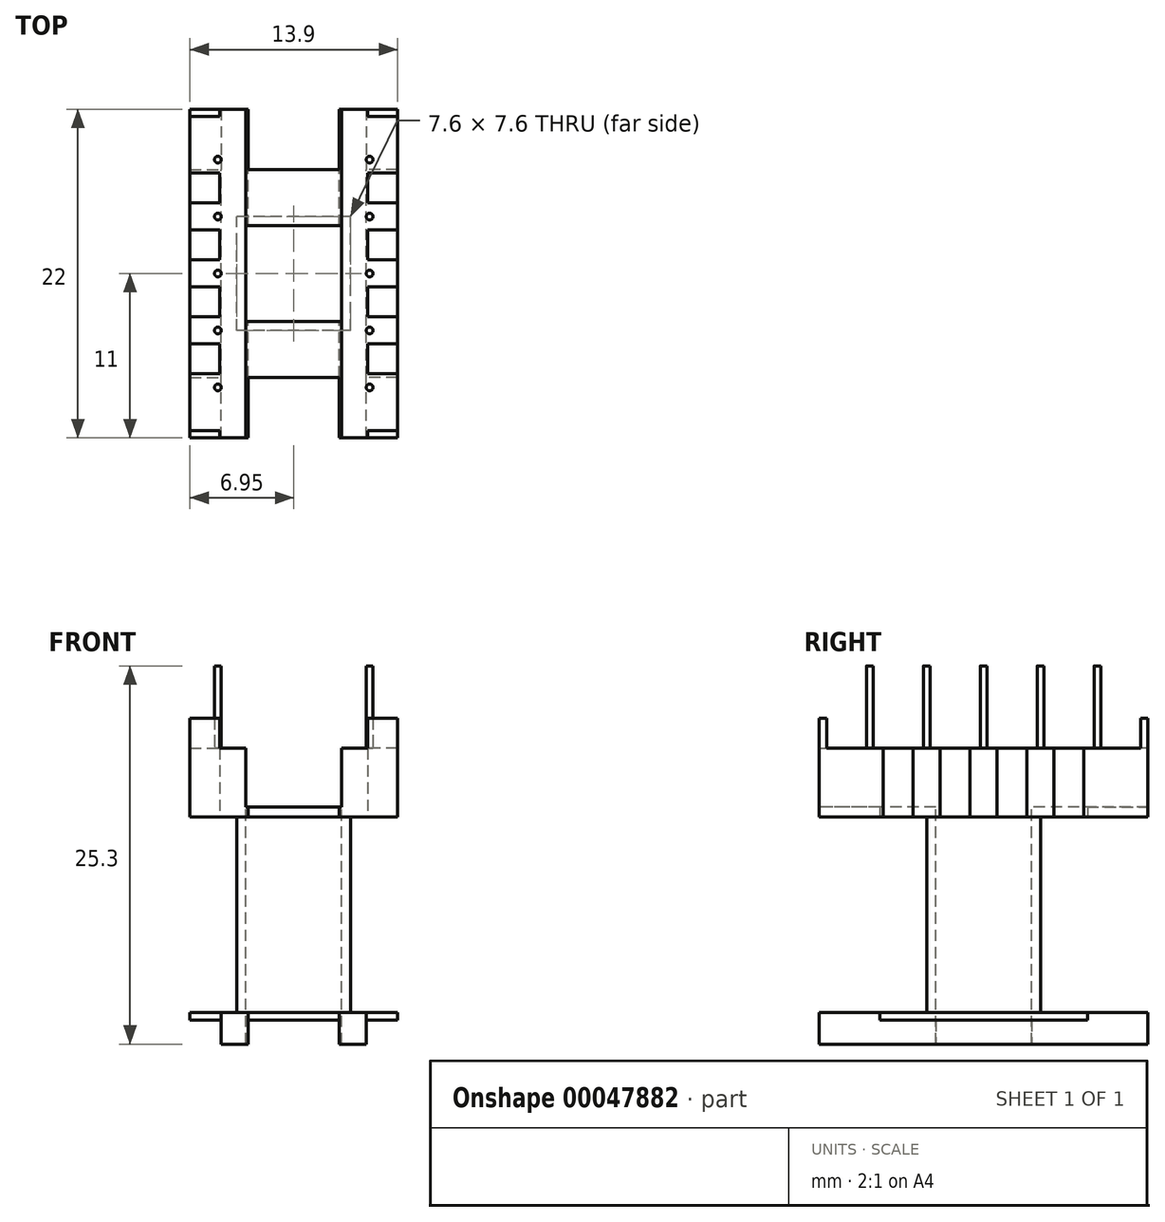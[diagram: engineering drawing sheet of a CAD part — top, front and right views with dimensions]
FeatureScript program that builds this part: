
annotation { "Feature Type Name" : "Feature", "Feature Type Description" : "" }
export const myFeature = defineFeature(function(context is Context, id is Id, definition is map)
    precondition{}
    {
        {
            var Q0;
            Q0=qCreatedBy(makeId("Top.planeOp"),FACE);
            var sketch = newSketch(context, id + "F0", { "sketchPlane" : qUnion([Q0])});
            skLineSegment(sketch, "E0.bottom", {"start": v(-6.95, -11) * mm, "end": v(6.95, -11) * mm});
            skLineSegment(sketch, "E0.top", {"start": v(-6.95, 11) * mm, "end": v(6.95, 11) * mm});
            skLineSegment(sketch, "E0.left", {"start": v(-6.95, -11) * mm, "end": v(-6.95, 11) * mm});
            skLineSegment(sketch, "E0.right", {"start": v(6.95, -11) * mm, "end": v(6.95, 11) * mm});
            skSolve(sketch);
        }
        {
            var Q0;
            Q0 = qSketchRegion(id + "F0", true);
            extrude(context, id + "F1", {"entities" : qUnion([Q0]), "depth" : 19.8 * mm});
        }
        {
            var Q0;
            Q0=makeQuery(id+"F1.opExtrude","CAP_FACE",FACE,{"disambiguationData":[OSD([sQuery(id+"F0.wireOp",EDGE,"E0.bottom"),sQuery(id+"F0.wireOp",EDGE,"E0.top"),sQuery(id+"F0.wireOp",EDGE,"E0.left"),sQuery(id+"F0.wireOp",EDGE,"E0.right")])],"isStart":true});
            cPlane(context, id + "F2", {"entities" : qUnion([Q0]), "cplaneType" : CPlaneType.OFFSET, "offset" : 2.1 * mm, "oppositeDirection" : true, "width" : 150 * mm, "height" : 150 * mm});
        }
        {
            var Q0;
            Q0=qCreatedBy(id+"F2.planeOp",FACE);
            cPlane(context, id + "F3", {"entities" : qUnion([Q0]), "cplaneType" : CPlaneType.OFFSET, "offset" : 13.1 * mm, "oppositeDirection" : true, "width" : 150 * mm, "height" : 150 * mm});
        }
        {
            var Q0;
            Q0=qCreatedBy(id+"F2.planeOp",FACE);
            var sketch = newSketch(context, id + "F4", { "sketchPlane" : qUnion([Q0])});
            skLineSegment(sketch, "E1.bottom", {"start": v(-3.8, -3.8) * mm, "end": v(3.8, -3.8) * mm});
            skLineSegment(sketch, "E1.top", {"start": v(-3.8, 3.8) * mm, "end": v(3.8, 3.8) * mm});
            skLineSegment(sketch, "E1.left", {"start": v(-3.8, -3.8) * mm, "end": v(-3.8, 3.8) * mm});
            skLineSegment(sketch, "E1.right", {"start": v(3.8, -3.8) * mm, "end": v(3.8, 3.8) * mm});
            skLineSegment(sketch, "E2.0", {"start": v(6.95, 11) * mm, "end": v(6.95, -11) * mm});
            skLineSegment(sketch, "E3.0", {"start": v(-6.95, 11) * mm, "end": v(6.95, 11) * mm});
            skLineSegment(sketch, "E4.0.0", {"start": v(-6.95, -11) * mm, "end": v(-6.95, 11) * mm});
            skLineSegment(sketch, "E4.0.2", {"start": v(-6.95, 11) * mm, "end": v(-6.95, -11) * mm});
            skLineSegment(sketch, "E4.1.2", {"start": v(6.95, 11) * mm, "end": v(-6.95, 11) * mm});
            skLineSegment(sketch, "E4.2.2", {"start": v(6.95, -11) * mm, "end": v(6.95, 11) * mm});
            skLineSegment(sketch, "E4.3.0", {"start": v(6.95, -11) * mm, "end": v(-6.95, -11) * mm});
            skLineSegment(sketch, "E4.3.2", {"start": v(-6.95, -11) * mm, "end": v(6.95, -11) * mm});
            skSolve(sketch);
        }
        {
            var Q0;
            Q0 = qSketchRegion(id + "F4", true);
            var Q1;
            Q1=qCreatedBy(id+"F3.planeOp",FACE);
            extrude(context, id + "F5", {"entities" : qUnion([Q0]), "operationType" : NewBodyOperationType.REMOVE, "endBound" : BoundingType.UP_TO_SURFACE, "oppositeDirection" : true, "endBoundEntityFace" : qUnion([Q1]), "depth" : 25 * mm});
        }
        {
            var Q0;
            Q0=makeQuery(id+"F1.opExtrude","CAP_FACE",FACE,{"disambiguationData":[OSD([sQuery(id+"F0.wireOp",EDGE,"E0.bottom"),sQuery(id+"F0.wireOp",EDGE,"E0.top"),sQuery(id+"F0.wireOp",EDGE,"E0.left"),sQuery(id+"F0.wireOp",EDGE,"E0.right")])],"isStart":false});
            var sketch = newSketch(context, id + "F6", { "sketchPlane" : qUnion([Q0])});
            skLineSegment(sketch, "E5.0.3", {"start": v(-3.8, 3.8) * mm, "end": v(3.8, 3.8) * mm, "construction": true});
            skLineSegment(sketch, "E5.1.2", {"start": v(-3.8, 3.8) * mm, "end": v(-3.8, -3.8) * mm, "construction": true});
            skLineSegment(sketch, "E5.2.2", {"start": v(-3.8, -3.8) * mm, "end": v(3.8, -3.8) * mm, "construction": true});
            skLineSegment(sketch, "E5.3.3", {"start": v(3.8, 3.8) * mm, "end": v(3.8, -3.8) * mm, "construction": true});
            skLineSegment(sketch, "E6.0", {"start": v(-3.2, 3.2) * mm, "end": v(-3.2, -3.2) * mm});
            skLineSegment(sketch, "E6.1", {"start": v(-3.2, 3.2) * mm, "end": v(3.2, 3.2) * mm});
            skLineSegment(sketch, "E6.2", {"start": v(3.2, 3.2) * mm, "end": v(3.2, -3.2) * mm});
            skLineSegment(sketch, "E6.3", {"start": v(-3.2, -3.2) * mm, "end": v(3.2, -3.2) * mm});
            skSolve(sketch);
        }
        {
            var Q0;
            Q0 = qSketchRegion(id + "F6", true);
            var Q1;
            Q1 = qConstructionFilter(qBodyType(qCreatedBy(id + "F6" ,EDGE), BodyType.WIRE), ConstructionObject.NO);
            extrude(context, id + "F7", {"entities" : qUnion([Q0]), "operationType" : NewBodyOperationType.REMOVE, "surfaceEntities" : qUnion([Q1]), "endBound" : BoundingType.THROUGH_ALL, "oppositeDirection" : true, "depth" : 25 * mm});
        }
        {
            var Q0;
            Q0=makeQuery(id+"F1.opExtrude","CAP_FACE",FACE,{"disambiguationData":[OSD([sQuery(id+"F0.wireOp",EDGE,"E0.bottom"),sQuery(id+"F0.wireOp",EDGE,"E0.top"),sQuery(id+"F0.wireOp",EDGE,"E0.left"),sQuery(id+"F0.wireOp",EDGE,"E0.right")])],"isStart":true});
            var sketch = newSketch(context, id + "F8", { "sketchPlane" : qUnion([Q0])});
            skLineSegment(sketch, "E7.0", {"start": v(-6.95, 11) * mm, "end": v(6.95, 11) * mm, "construction": true});
            skLineSegment(sketch, "E8.0", {"start": v(-6.95, -11) * mm, "end": v(6.95, -11) * mm, "construction": true});
            skLineSegment(sketch, "E9.0.1", {"start": v(6.95, 11) * mm, "end": v(-6.95, 11) * mm, "construction": true});
            skLineSegment(sketch, "E10.0.3", {"start": v(6.95, -11) * mm, "end": v(-6.95, -11) * mm, "construction": true});
            skLineSegment(sketch, "E11.0.1", {"start": v(-6.95, 11) * mm, "end": v(-6.95, -11) * mm, "construction": true});
            skLineSegment(sketch, "E11.0.3", {"start": v(-6.95, -11) * mm, "end": v(-6.95, 11) * mm, "construction": true});
            skLineSegment(sketch, "E12.0.1", {"start": v(6.95, -11) * mm, "end": v(6.95, 11) * mm, "construction": true});
            skLineSegment(sketch, "E12.0.3", {"start": v(6.95, 11) * mm, "end": v(6.95, -11) * mm, "construction": true});
            skLineSegment(sketch, "E13.bottom", {"start": v(-4.85, 11) * mm, "end": v(-3.05, 11) * mm, "construction": true});
            skLineSegment(sketch, "E13.top", {"start": v(-4.85, -11) * mm, "end": v(-3.05, -11) * mm, "construction": true});
            skLineSegment(sketch, "E13.left", {"start": v(-4.85, 11) * mm, "end": v(-4.85, -11) * mm});
            skLineSegment(sketch, "E13.right", {"start": v(-3.05, 11) * mm, "end": v(-3.05, -11) * mm});
            skLineSegment(sketch, "E14.bottom", {"start": v(3.05, 11) * mm, "end": v(4.85, 11) * mm, "construction": true});
            skLineSegment(sketch, "E14.top", {"start": v(3.05, -11) * mm, "end": v(4.85, -11) * mm, "construction": true});
            skLineSegment(sketch, "E14.left", {"start": v(3.05, 11) * mm, "end": v(3.05, -11) * mm});
            skLineSegment(sketch, "E14.right", {"start": v(4.85, 11) * mm, "end": v(4.85, -11) * mm});
            skLineSegment(sketch, "E15", {"start": v(-3.05, 11) * mm, "end": v(3.05, 11) * mm});
            skLineSegment(sketch, "E16", {"start": v(-3.05, -11) * mm, "end": v(3.05, -11) * mm});
            skLineSegment(sketch, "E17", {"start": v(4.85, -11) * mm, "end": v(6.95, -11) * mm});
            skLineSegment(sketch, "E18", {"start": v(6.95, 11) * mm, "end": v(6.95, -11) * mm});
            skLineSegment(sketch, "E19", {"start": v(6.95, 11) * mm, "end": v(4.85, 11) * mm});
            skLineSegment(sketch, "E20", {"start": v(-4.85, 11) * mm, "end": v(-6.95, 11) * mm});
            skLineSegment(sketch, "E21", {"start": v(-6.95, 11) * mm, "end": v(-6.95, -11) * mm});
            skLineSegment(sketch, "E22", {"start": v(-6.95, -11) * mm, "end": v(-4.85, -11) * mm});
            skSolve(sketch);
        }
        {
            var Q0;
            Q0 = qSketchRegion(id + "F8", true);
            var Q1;
            Q1=sQuery(id+"F8.wireOp",EDGE,"E13.bottom");
            var Q2;
            Q2=sQuery(id+"F8.wireOp",EDGE,"E13.top");
            var Q3;
            Q3=sQuery(id+"F8.wireOp",EDGE,"E14.bottom");
            var Q4;
            Q4=sQuery(id+"F8.wireOp",EDGE,"E14.top");
            var Q5;
            Q5=makeQuery(id+"F5.boolean.opBoolean","COPY",FACE,{"derivedFrom":makeQuery(id+"F5.opExtrude","CAP_FACE",FACE,{"disambiguationData":[OSD([sQuery(id+"F4.wireOp",EDGE,"E1.bottom"),sQuery(id+"F4.wireOp",EDGE,"E1.top"),sQuery(id+"F4.wireOp",EDGE,"E1.left"),sQuery(id+"F4.wireOp",EDGE,"E1.right"),sQuery(id+"F4.wireOp",EDGE,"E4.0.2"),sQuery(id+"F4.wireOp",EDGE,"E4.1.2"),sQuery(id+"F4.wireOp",EDGE,"E4.2.2"),sQuery(id+"F4.wireOp",EDGE,"E4.3.2")])],"isStart":true})});
            extrude(context, id + "F9", {"entities" : qUnion([Q0]), "operationType" : NewBodyOperationType.REMOVE, "surfaceEntities" : qUnion([Q1, Q2, Q3, Q4]), "oppositeDirection" : true, "endBoundEntityFace" : qUnion([Q5]), "depth" : 1.6 * mm});
        }
        {
            var Q0;
            Q0=makeQuery(id+"F5.boolean.opBoolean","COPY",FACE,{"derivedFrom":makeQuery(id+"F5.opExtrude","CAP_FACE",FACE,{"disambiguationData":[OSD([sQuery(id+"F4.wireOp",EDGE,"E1.bottom"),sQuery(id+"F4.wireOp",EDGE,"E1.top"),sQuery(id+"F4.wireOp",EDGE,"E1.left"),sQuery(id+"F4.wireOp",EDGE,"E1.right"),sQuery(id+"F4.wireOp",EDGE,"E4.0.2"),sQuery(id+"F4.wireOp",EDGE,"E4.1.2"),sQuery(id+"F4.wireOp",EDGE,"E4.2.2"),sQuery(id+"F4.wireOp",EDGE,"E4.3.2")])],"isStart":true})});
            var sketch = newSketch(context, id + "F10", { "sketchPlane" : qUnion([Q0])});
            skPoint(sketch, "E23.0", {"position": v(6.95, 11) * mm});
            skPoint(sketch, "E23.1", {"position": v(4.85, 11) * mm});
            skPoint(sketch, "E23.2", {"position": v(3.05, 11) * mm});
            skPoint(sketch, "E23.3", {"position": v(-3.05, 11) * mm});
            skPoint(sketch, "E23.4", {"position": v(-4.85, 11) * mm});
            skPoint(sketch, "E23.5", {"position": v(-6.95, 11) * mm});
            skPoint(sketch, "E23.6", {"position": v(6.95, -11) * mm});
            skPoint(sketch, "E23.7", {"position": v(4.85, -11) * mm});
            skPoint(sketch, "E23.8", {"position": v(3.05, -11) * mm});
            skPoint(sketch, "E23.9", {"position": v(-4.85, -11) * mm});
            skPoint(sketch, "E23.10", {"position": v(-6.95, -11) * mm});
            skPoint(sketch, "E23.11", {"position": v(-3.05, -11) * mm});
            skLineSegment(sketch, "E24.bottom", {"start": v(6.95, 11) * mm, "end": v(4.85, 11) * mm});
            skLineSegment(sketch, "E24.top", {"start": v(6.95, 6.95) * mm, "end": v(4.85, 6.95) * mm});
            skLineSegment(sketch, "E24.left", {"start": v(6.95, 11) * mm, "end": v(6.95, 6.95) * mm});
            skLineSegment(sketch, "E24.right", {"start": v(4.85, 11) * mm, "end": v(4.85, 6.95) * mm});
            skLineSegment(sketch, "E25.bottom", {"start": v(6.95, -11) * mm, "end": v(4.85, -11) * mm});
            skLineSegment(sketch, "E25.top", {"start": v(6.95, -6.95) * mm, "end": v(4.85, -6.95) * mm});
            skLineSegment(sketch, "E25.left", {"start": v(6.95, -11) * mm, "end": v(6.95, -6.95) * mm});
            skLineSegment(sketch, "E25.right", {"start": v(4.85, -11) * mm, "end": v(4.85, -6.95) * mm});
            skLineSegment(sketch, "E26.bottom", {"start": v(3.05, -11) * mm, "end": v(-3.05, -11) * mm});
            skLineSegment(sketch, "E26.top", {"start": v(3.05, -6.95) * mm, "end": v(-3.05, -6.95) * mm});
            skLineSegment(sketch, "E26.left", {"start": v(3.05, -11) * mm, "end": v(3.05, -6.95) * mm});
            skLineSegment(sketch, "E26.right", {"start": v(-3.05, -11) * mm, "end": v(-3.05, -6.95) * mm});
            skLineSegment(sketch, "E27.bottom", {"start": v(-6.95, -11) * mm, "end": v(-4.85, -11) * mm});
            skLineSegment(sketch, "E27.top", {"start": v(-6.95, -6.95) * mm, "end": v(-4.85, -6.95) * mm});
            skLineSegment(sketch, "E27.left", {"start": v(-6.95, -11) * mm, "end": v(-6.95, -6.95) * mm});
            skLineSegment(sketch, "E27.right", {"start": v(-4.85, -11) * mm, "end": v(-4.85, -6.95) * mm});
            skLineSegment(sketch, "E28.bottom", {"start": v(-6.95, 11) * mm, "end": v(-4.85, 11) * mm});
            skLineSegment(sketch, "E28.top", {"start": v(-6.95, 6.95) * mm, "end": v(-4.85, 6.95) * mm});
            skLineSegment(sketch, "E28.left", {"start": v(-6.95, 11) * mm, "end": v(-6.95, 6.95) * mm});
            skLineSegment(sketch, "E28.right", {"start": v(-4.85, 11) * mm, "end": v(-4.85, 6.95) * mm});
            skLineSegment(sketch, "E29.bottom", {"start": v(-3.05, 11) * mm, "end": v(3.05, 11) * mm});
            skLineSegment(sketch, "E29.top", {"start": v(-3.05, 6.95) * mm, "end": v(3.05, 6.95) * mm});
            skLineSegment(sketch, "E29.left", {"start": v(-3.05, 11) * mm, "end": v(-3.05, 6.95) * mm});
            skLineSegment(sketch, "E29.right", {"start": v(3.05, 11) * mm, "end": v(3.05, 6.95) * mm});
            skSolve(sketch);
        }
        {
            var Q0;
            Q0 = qSketchRegion(id + "F10", true);
            var Q1;
            Q1=makeQuery(id+"F9.boolean.opBoolean","COPY",FACE,{"disambiguationData":[OD(0.0)],"derivedFrom":makeQuery(id+"F9.opExtrude","CAP_FACE",FACE,{"disambiguationData":[OSD([sQuery(id+"F8.wireOp",EDGE,"E13.right"),sQuery(id+"F8.wireOp",EDGE,"E14.left"),sQuery(id+"F8.wireOp",EDGE,"E15"),sQuery(id+"F8.wireOp",EDGE,"E16")])],"isStart":false})});
            extrude(context, id + "F11", {"entities" : qUnion([Q0]), "operationType" : NewBodyOperationType.REMOVE, "endBound" : BoundingType.UP_TO_SURFACE, "oppositeDirection" : true, "endBoundEntityFace" : qUnion([Q1]), "depth" : 25 * mm});
        }
        {
            var Q0;
            Q0=makeQuery(id+"F5.boolean.opBoolean","COPY",FACE,{"derivedFrom":makeQuery(id+"F5.opExtrude","CAP_FACE",FACE,{"disambiguationData":[OSD([sQuery(id+"F4.wireOp",EDGE,"E1.bottom"),sQuery(id+"F4.wireOp",EDGE,"E1.top"),sQuery(id+"F4.wireOp",EDGE,"E1.left"),sQuery(id+"F4.wireOp",EDGE,"E1.right"),sQuery(id+"F4.wireOp",EDGE,"E4.0.2"),sQuery(id+"F4.wireOp",EDGE,"E4.1.2"),sQuery(id+"F4.wireOp",EDGE,"E4.2.2"),sQuery(id+"F4.wireOp",EDGE,"E4.3.2")])],"isStart":false})});
            var sketch = newSketch(context, id + "F12", { "sketchPlane" : qUnion([Q0])});
            skPoint(sketch, "E30.0", {"position": v(6.95, -11) * mm});
            skPoint(sketch, "E30.1", {"position": v(-6.95, -11) * mm});
            skPoint(sketch, "E30.2", {"position": v(6.95, 11) * mm});
            skPoint(sketch, "E30.3", {"position": v(-6.95, 11) * mm});
            skPoint(sketch, "E30.5", {"position": v(3.05, 6.95) * mm});
            skPoint(sketch, "E30.6", {"position": v(3.05, -6.95) * mm});
            skPoint(sketch, "E30.7", {"position": v(-3.05, -6.95) * mm});
            skLineSegment(sketch, "E31.bottom", {"start": v(-3.05, -6.95) * mm, "end": v(3.05, -6.95) * mm});
            skLineSegment(sketch, "E31.top", {"start": v(-3.05, -11) * mm, "end": v(3.05, -11) * mm});
            skLineSegment(sketch, "E31.left", {"start": v(-3.05, -6.95) * mm, "end": v(-3.05, -11) * mm});
            skLineSegment(sketch, "E31.right", {"start": v(3.05, -6.95) * mm, "end": v(3.05, -11) * mm});
            skLineSegment(sketch, "E32", {"start": v(-6.95, 11) * mm, "end": v(-6.95, -11) * mm, "construction": true});
            skLineSegment(sketch, "E33.bottom", {"start": v(6.95, -6.72) * mm, "end": v(4.95, -6.72) * mm});
            skLineSegment(sketch, "E33.top", {"start": v(6.95, -4.72) * mm, "end": v(4.95, -4.72) * mm});
            skLineSegment(sketch, "E33.left", {"start": v(6.95, -6.72) * mm, "end": v(6.95, -4.72) * mm});
            skLineSegment(sketch, "E33.right", {"start": v(4.95, -6.72) * mm, "end": v(4.95, -4.72) * mm});
            skLineSegment(sketch, "E34.bottom", {"start": v(6.95, -2.9) * mm, "end": v(4.95, -2.9) * mm});
            skLineSegment(sketch, "E34.top", {"start": v(6.95, -0.9) * mm, "end": v(4.95, -0.9) * mm});
            skLineSegment(sketch, "E34.left", {"start": v(6.95, -2.9) * mm, "end": v(6.95, -0.9) * mm});
            skLineSegment(sketch, "E34.right", {"start": v(4.95, -2.9) * mm, "end": v(4.95, -0.9) * mm});
            skLineSegment(sketch, "E35.bottom", {"start": v(6.95, 0.9) * mm, "end": v(4.95, 0.9) * mm});
            skLineSegment(sketch, "E35.top", {"start": v(6.95, 2.9) * mm, "end": v(4.95, 2.9) * mm});
            skLineSegment(sketch, "E35.left", {"start": v(6.95, 0.9) * mm, "end": v(6.95, 2.9) * mm});
            skLineSegment(sketch, "E35.right", {"start": v(4.95, 0.9) * mm, "end": v(4.95, 2.9) * mm});
            skLineSegment(sketch, "E36.bottom", {"start": v(6.95, 4.72) * mm, "end": v(4.95, 4.72) * mm});
            skLineSegment(sketch, "E36.top", {"start": v(6.95, 6.72) * mm, "end": v(4.95, 6.72) * mm});
            skLineSegment(sketch, "E36.left", {"start": v(6.95, 4.72) * mm, "end": v(6.95, 6.72) * mm});
            skLineSegment(sketch, "E36.right", {"start": v(4.95, 4.72) * mm, "end": v(4.95, 6.72) * mm});
            skLineSegment(sketch, "E37", {"start": v(6.95, -4.72) * mm, "end": v(6.95, -2.9) * mm, "construction": true});
            skLineSegment(sketch, "E38", {"start": v(6.95, -0.9) * mm, "end": v(6.95, 0.9) * mm, "construction": true});
            skLineSegment(sketch, "E39", {"start": v(6.95, 2.9) * mm, "end": v(6.95, 4.72) * mm, "construction": true});
            skLineSegment(sketch, "E40.bottom", {"start": v(-6.95, 6.72) * mm, "end": v(-4.95, 6.72) * mm});
            skLineSegment(sketch, "E40.top", {"start": v(-6.95, 4.72) * mm, "end": v(-4.95, 4.72) * mm});
            skLineSegment(sketch, "E40.left", {"start": v(-6.95, 6.72) * mm, "end": v(-6.95, 4.72) * mm});
            skLineSegment(sketch, "E40.right", {"start": v(-4.95, 6.72) * mm, "end": v(-4.95, 4.72) * mm});
            skPoint(sketch, "E41.0", {"position": v(-3.05, 6.95) * mm});
            skLineSegment(sketch, "E42.bottom", {"start": v(3.05, 6.95) * mm, "end": v(-3.05, 6.95) * mm});
            skLineSegment(sketch, "E42.top", {"start": v(3.05, 11) * mm, "end": v(-3.05, 11) * mm});
            skLineSegment(sketch, "E42.left", {"start": v(3.05, 6.95) * mm, "end": v(3.05, 11) * mm});
            skLineSegment(sketch, "E42.right", {"start": v(-3.05, 6.95) * mm, "end": v(-3.05, 11) * mm});
            skLineSegment(sketch, "E43.bottom", {"start": v(-6.95, 2.9) * mm, "end": v(-4.95, 2.9) * mm});
            skLineSegment(sketch, "E43.top", {"start": v(-6.95, 0.9) * mm, "end": v(-4.95, 0.9) * mm});
            skLineSegment(sketch, "E43.left", {"start": v(-6.95, 2.9) * mm, "end": v(-6.95, 0.9) * mm});
            skLineSegment(sketch, "E43.right", {"start": v(-4.95, 2.9) * mm, "end": v(-4.95, 0.9) * mm});
            skLineSegment(sketch, "E44.bottom", {"start": v(-6.95, -0.9) * mm, "end": v(-4.95, -0.9) * mm});
            skLineSegment(sketch, "E44.top", {"start": v(-6.95, -2.9) * mm, "end": v(-4.95, -2.9) * mm});
            skLineSegment(sketch, "E44.left", {"start": v(-6.95, -0.9) * mm, "end": v(-6.95, -2.9) * mm});
            skLineSegment(sketch, "E44.right", {"start": v(-4.95, -0.9) * mm, "end": v(-4.95, -2.9) * mm});
            skLineSegment(sketch, "E45.bottom", {"start": v(-6.95, -4.72) * mm, "end": v(-4.95, -4.72) * mm});
            skLineSegment(sketch, "E45.top", {"start": v(-6.95, -6.72) * mm, "end": v(-4.95, -6.72) * mm});
            skLineSegment(sketch, "E45.left", {"start": v(-6.95, -4.72) * mm, "end": v(-6.95, -6.72) * mm});
            skLineSegment(sketch, "E45.right", {"start": v(-4.95, -4.72) * mm, "end": v(-4.95, -6.72) * mm});
            skLineSegment(sketch, "E46", {"start": v(-6.95, 4.72) * mm, "end": v(-6.95, 2.9) * mm, "construction": true});
            skLineSegment(sketch, "E47", {"start": v(-6.95, 0.9) * mm, "end": v(-6.95, -0.9) * mm, "construction": true});
            skLineSegment(sketch, "E48", {"start": v(-6.95, -2.9) * mm, "end": v(-6.95, -4.72) * mm, "construction": true});
            skLineSegment(sketch, "E49", {"start": v(-6.95, 2.9) * mm, "end": v(-6.95, 4.72) * mm, "construction": true});
            skSolve(sketch);
        }
        {
            var Q0;
            Q0 = qSketchRegion(id + "F12", true);
            var Q1;
            Q1=makeQuery(id+"F1.opExtrude","CAP_FACE",FACE,{"disambiguationData":[OSD([sQuery(id+"F0.wireOp",EDGE,"E0.bottom"),sQuery(id+"F0.wireOp",EDGE,"E0.top"),sQuery(id+"F0.wireOp",EDGE,"E0.left"),sQuery(id+"F0.wireOp",EDGE,"E0.right")])],"isStart":false});
            extrude(context, id + "F13", {"entities" : qUnion([Q0]), "operationType" : NewBodyOperationType.REMOVE, "endBound" : BoundingType.UP_TO_SURFACE, "oppositeDirection" : true, "endBoundEntityFace" : qUnion([Q1]), "depth" : 25 * mm});
        }
        {
            var Q0;
            Q0=qCreatedBy(makeId("Front.planeOp"),FACE);
            var sketch = newSketch(context, id + "F14", { "sketchPlane" : qUnion([Q0])});
            skLineSegment(sketch, "E50.bottom", {"start": v(3.2, 15.85) * mm, "end": v(-3.2, 15.85) * mm});
            skLineSegment(sketch, "E50.top", {"start": v(3.2, 19.8) * mm, "end": v(-3.2, 19.8) * mm});
            skLineSegment(sketch, "E50.left", {"start": v(3.2, 15.85) * mm, "end": v(3.2, 19.8) * mm});
            skLineSegment(sketch, "E50.right", {"start": v(-3.2, 15.85) * mm, "end": v(-3.2, 19.8) * mm});
            skPoint(sketch, "E51.0", {"position": v(-3.2, 19.8) * mm});
            skPoint(sketch, "E51.1", {"position": v(3.2, 19.8) * mm});
            skPoint(sketch, "E52.0", {"position": v(-3.05, 15.2) * mm});
            skPoint(sketch, "E52.1", {"position": v(3.05, 15.2) * mm});
            skSolve(sketch);
        }
        {
            var Q0;
            Q0 = qSketchRegion(id + "F14", true);
            extrude(context, id + "F15", {"entities" : qUnion([Q0]), "operationType" : NewBodyOperationType.REMOVE, "endBound" : BoundingType.THROUGH_ALL, "oppositeDirection" : true, "depth" : 25 * mm, "hasSecondDirection" : true, "secondDirectionBound" : SecondDirectionBoundingType.THROUGH_ALL, "secondDirectionOppositeDirection" : false, "secondDirectionDepth" : 25 * mm});
        }
        {
            var Q0;
            {var subQ0=sQuery(id+"F0.wireOp",EDGE,"E0.bottom");var subQ1=sQuery(id+"F0.wireOp",EDGE,"E0.top");var subQ2=sQuery(id+"F0.wireOp",EDGE,"E0.right");Q0=makeQuery(id+"F15.boolean.opBoolean","SPLIT",FACE,{"disambiguationData":[TD([makeQuery(id+"F1.opExtrude","SWEPT_FACE",FACE,{"disambiguationData":[OSD([subQ2])]})])],"derivedFrom":makeQuery(id+"F1.opExtrude","CAP_FACE",FACE,{"disambiguationData":[OSD([subQ0,subQ1,sQuery(id+"F0.wireOp",EDGE,"E0.left"),subQ2])],"isStart":false})});}
            var sketch = newSketch(context, id + "F16", { "sketchPlane" : qUnion([Q0])});
            skLineSegment(sketch, "E53", {"start": v(-5.08, -11) * mm, "end": v(-5.08, 11) * mm, "construction": true});
            skLineSegment(sketch, "E54", {"start": v(5.08, -11) * mm, "end": v(5.08, 11) * mm, "construction": true});
            skLineSegment(sketch, "E55", {"start": v(6.95, 3.81) * mm, "end": v(-5.08, 3.81) * mm, "construction": true});
            skLineSegment(sketch, "E56", {"start": v(6.95, 0) * mm, "end": v(-5.08, 0) * mm, "construction": true});
            skLineSegment(sketch, "E57", {"start": v(6.95, -3.81) * mm, "end": v(-5.08, -3.81) * mm, "construction": true});
            skLineSegment(sketch, "E58", {"start": v(5.08, 7.62) * mm, "end": v(-5.08, 7.62) * mm, "construction": true});
            skLineSegment(sketch, "E59", {"start": v(5.08, -7.62) * mm, "end": v(-5.08, -7.62) * mm, "construction": true});
            skLineSegment(sketch, "E60", {"start": v(5.08, 0) * mm, "end": v(5.08, 3.81) * mm, "construction": true});
            skLineSegment(sketch, "E61", {"start": v(5.08, 3.81) * mm, "end": v(5.08, 7.62) * mm, "construction": true});
            skLineSegment(sketch, "E62", {"start": v(5.08, -7.62) * mm, "end": v(5.08, -3.81) * mm, "construction": true});
            skCircle(sketch, "E63", {"center": v(5.08, 7.62) * mm, "radius": 0.23 * mm});
            skCircle(sketch, "E64", {"center": v(5.08, 3.81) * mm, "radius": 0.23 * mm});
            skCircle(sketch, "E65", {"center": v(5.08, 0) * mm, "radius": 0.23 * mm});
            skCircle(sketch, "E66", {"center": v(5.08, -3.81) * mm, "radius": 0.23 * mm});
            skCircle(sketch, "E67", {"center": v(5.08, -7.62) * mm, "radius": 0.23 * mm});
            skCircle(sketch, "E68", {"center": v(-5.08, -7.62) * mm, "radius": 0.23 * mm});
            skCircle(sketch, "E69", {"center": v(-5.08, -3.81) * mm, "radius": 0.23 * mm});
            skCircle(sketch, "E70", {"center": v(-5.08, 0) * mm, "radius": 0.23 * mm});
            skCircle(sketch, "E71", {"center": v(-5.08, 3.81) * mm, "radius": 0.23 * mm});
            skCircle(sketch, "E72", {"center": v(-5.08, 7.62) * mm, "radius": 0.23 * mm});
            skSolve(sketch);
        }
        {
            var Q0;
            Q0 = qSketchRegion(id + "F16", true);
            extrude(context, id + "F17", {"entities" : qUnion([Q0]), "operationType" : NewBodyOperationType.ADD, "depth" : 5.5 * mm});
        }
        {
            var Q0;
            {var subQ0=sQuery(id+"F0.wireOp",EDGE,"E0.bottom");var subQ1=sQuery(id+"F0.wireOp",EDGE,"E0.top");var subQ2=sQuery(id+"F0.wireOp",EDGE,"E0.left");Q0=makeQuery(id+"F15.boolean.opBoolean","SPLIT",FACE,{"disambiguationData":[TD([makeQuery(id+"F1.opExtrude","SWEPT_FACE",FACE,{"disambiguationData":[OSD([subQ2])]})])],"derivedFrom":makeQuery(id+"F1.opExtrude","CAP_FACE",FACE,{"disambiguationData":[OSD([subQ0,subQ1,subQ2,sQuery(id+"F0.wireOp",EDGE,"E0.right")])],"isStart":false})});}
            var sketch = newSketch(context, id + "F18", { "sketchPlane" : qUnion([Q0])});
            skLineSegment(sketch, "E73.bottom", {"start": v(-6.95, 11) * mm, "end": v(-4.95, 11) * mm});
            skLineSegment(sketch, "E73.top", {"start": v(-6.95, 10.5) * mm, "end": v(-4.95, 10.5) * mm});
            skLineSegment(sketch, "E73.left", {"start": v(-6.95, 11) * mm, "end": v(-6.95, 10.5) * mm});
            skLineSegment(sketch, "E73.right", {"start": v(-4.95, 11) * mm, "end": v(-4.95, 10.5) * mm});
            skLineSegment(sketch, "E74.bottom", {"start": v(-6.95, -11) * mm, "end": v(-4.95, -11) * mm});
            skLineSegment(sketch, "E74.top", {"start": v(-6.95, -10.5) * mm, "end": v(-4.95, -10.5) * mm});
            skLineSegment(sketch, "E74.left", {"start": v(-6.95, -11) * mm, "end": v(-6.95, -10.5) * mm});
            skLineSegment(sketch, "E74.right", {"start": v(-4.95, -11) * mm, "end": v(-4.95, -10.5) * mm});
            skLineSegment(sketch, "E75.bottom", {"start": v(6.95, -11) * mm, "end": v(4.95, -11) * mm});
            skLineSegment(sketch, "E75.top", {"start": v(6.95, -10.5) * mm, "end": v(4.95, -10.5) * mm});
            skLineSegment(sketch, "E75.left", {"start": v(6.95, -11) * mm, "end": v(6.95, -10.5) * mm});
            skLineSegment(sketch, "E75.right", {"start": v(4.95, -11) * mm, "end": v(4.95, -10.5) * mm});
            skLineSegment(sketch, "E76.bottom", {"start": v(6.95, 11) * mm, "end": v(4.95, 11) * mm});
            skLineSegment(sketch, "E76.top", {"start": v(6.95, 10.5) * mm, "end": v(4.95, 10.5) * mm});
            skLineSegment(sketch, "E76.left", {"start": v(6.95, 11) * mm, "end": v(6.95, 10.5) * mm});
            skLineSegment(sketch, "E76.right", {"start": v(4.95, 11) * mm, "end": v(4.95, 10.5) * mm});
            skSolve(sketch);
        }
        {
            var Q0;
            Q0 = qSketchRegion(id + "F18", true);
            extrude(context, id + "F19", {"entities" : qUnion([Q0]), "operationType" : NewBodyOperationType.ADD, "depth" : 2 * mm});
        }
    });
